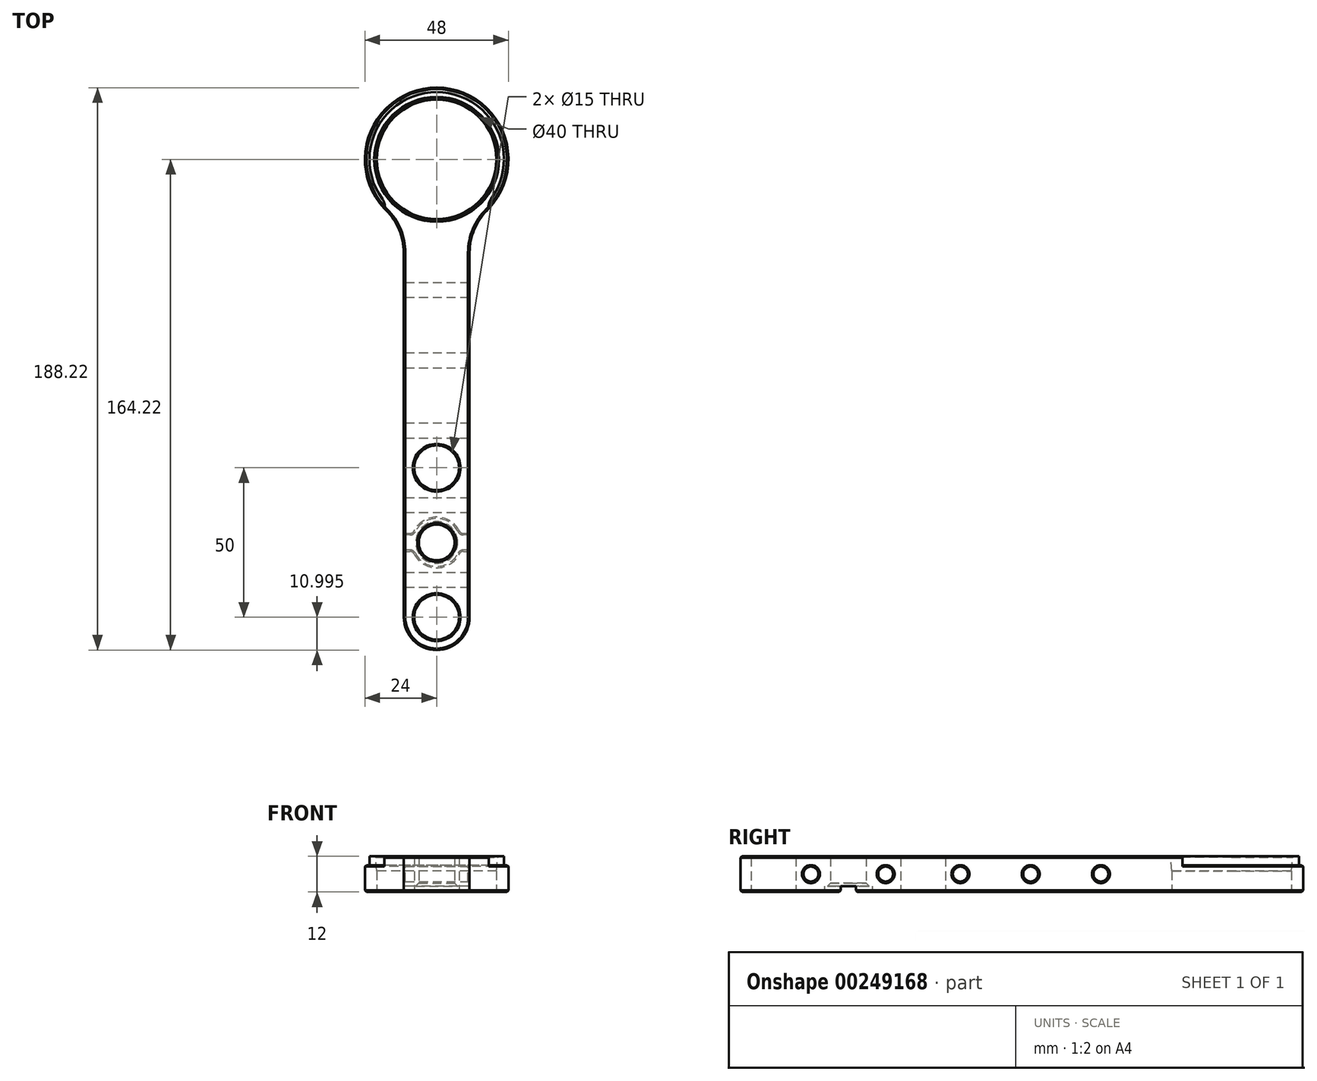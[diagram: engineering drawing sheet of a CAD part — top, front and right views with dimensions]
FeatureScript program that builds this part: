
annotation { "Feature Type Name" : "Feature", "Feature Type Description" : "" }
export const myFeature = defineFeature(function(context is Context, id is Id, definition is map)
    precondition{}
    {
        {
            var Q0;
            Q0=qCreatedBy(makeId("Top.planeOp"),FACE);
            var sketch = newSketch(context, id + "F0", { "sketchPlane" : qUnion([Q0])});
            skArc(sketch, "E0", {"start": v(0, 24) * mm, "mid": v(-22.19, 9.14) * mm, "end": v(-16.9, -17.03) * mm});
            skArc(sketch, "E1", {"start": v(0, 20) * mm, "mid": v(-20, 0) * mm, "end": v(0, -20) * mm});
            skLineSegment(sketch, "E2", {"start": v(0, 0) * mm, "end": v(0, 24) * mm, "construction": true});
            skArc(sketch, "E3.MirrorCS", {"start": v(0, 24) * mm, "mid": v(23.32, 5.66) * mm, "end": v(11, -21.33) * mm});
            skLineSegment(sketch, "E4.top", {"start": v(11, -91.22) * mm, "end": v(-11, -91.22) * mm, "construction": true});
            skLineSegment(sketch, "E4.left", {"start": v(11, -31.22) * mm, "end": v(11, -91.22) * mm});
            skLineSegment(sketch, "E4.right", {"start": v(-11, -31.22) * mm, "end": v(-11, -91.22) * mm});
            skArc(sketch, "E5.trimOffspring", {"start": v(-11, -21.33) * mm, "mid": v(-23.32, 5.66) * mm, "end": v(0, 24) * mm});
            skArc(sketch, "E6.trimOffspring", {"start": v(16.9, -17.03) * mm, "mid": v(22.19, 9.14) * mm, "end": v(0, 24) * mm});
            skPoint(sketch, "E7.visualSharp", {"position": v(-11, -21.33) * mm});
            skArc(sketch, "E7.filletArc", {"start": v(-11, -31.22) * mm, "mid": v(-12.54, -23.54) * mm, "end": v(-16.9, -17.03) * mm});
            skPoint(sketch, "E8.visualSharp", {"position": v(11, -21.33) * mm});
            skArc(sketch, "E8.filletArc", {"start": v(16.9, -17.03) * mm, "mid": v(12.54, -23.54) * mm, "end": v(11, -31.22) * mm});
            skLineSegment(sketch, "E9", {"start": v(-11, -91.22) * mm, "end": v(-11, -153.22) * mm});
            skLineSegment(sketch, "E10", {"start": v(-11, -164.22) * mm, "end": v(11, -164.22) * mm, "construction": true});
            skLineSegment(sketch, "E11", {"start": v(11, -153.22) * mm, "end": v(11, -91.22) * mm});
            skLineSegment(sketch, "E12", {"start": v(0, -91.22) * mm, "end": v(0, -103.22) * mm, "construction": true});
            skPoint(sketch, "E12.endSnap0", {"position": v(0, -91.22) * mm});
            skLineSegment(sketch, "E13", {"start": v(0, -103.22) * mm, "end": v(0, -128.22) * mm, "construction": true});
            skLineSegment(sketch, "E14", {"start": v(0, -128.22) * mm, "end": v(0, -153.22) * mm, "construction": true});
            skCircle(sketch, "E15", {"center": v(0, -103.22) * mm, "radius": 7.5 * mm});
            skCircle(sketch, "E16", {"center": v(0, -153.22) * mm, "radius": 7.5 * mm});
            skPoint(sketch, "E17", {"position": v(0, -128.22) * mm});
            skArc(sketch, "E18", {"start": v(-11, -153.22) * mm, "mid": v(0, -164.22) * mm, "end": v(11, -153.22) * mm});
            skCircle(sketch, "E19", {"center": v(0, -128.22) * mm, "radius": 6 * mm});
            skArc(sketch, "E20.trimOffspring", {"start": v(0, -20) * mm, "mid": v(20, 0) * mm, "end": v(0, 20) * mm});
            skSolve(sketch);
        }
        {
            var Q0;
            Q0 = qSketchRegion(id + "F0", true);
            extrude(context, id + "F1", {"entities" : qUnion([Q0]), "depth" : 12 * mm});
        }
        {
            var Q0;
            Q0=makeQuery(id+"F1.opExtrude","CAP_FACE",FACE,{"disambiguationData":[OSD([sQuery(id+"F0.wireOp",EDGE,"E1"),sQuery(id+"F0.wireOp",EDGE,"F11VOZdt-HZaE-PrO8-QXOm-NcNPcNM7g2nS"),sQuery(id+"F0.wireOp",EDGE,"7m6biw3m-Naaw-kAyD-0goq-zmuKVY0ows0u"),sQuery(id+"F0.wireOp",EDGE,"G1YBRX1K-NmOF-07IS-Nktl-OATFWiHAXenz"),sQuery(id+"F0.wireOp",EDGE,"hBhdh0xz-QFaw-vZRR-R82u-J2mHWQ1tEoxB"),sQuery(id+"F0.wireOp",EDGE,"4GYq8nPm-MSU2-L5ly-pOQU-XlYa1snlLOT1"),sQuery(id+"F0.wireOp",EDGE,"5b97e5dd-33e6-46e9-ad2f-97bc99eada040.MirrorCS"),sQuery(id+"F0.wireOp",EDGE,"66a7403b-aaa3-430a-aa9c-4d805a2a6571.filletArc"),sQuery(id+"F0.wireOp",EDGE,"590532eb-86fd-4acb-be48-ccb052db704c0.MirrorCS"),sQuery(id+"F0.wireOp",EDGE,"590532eb-86fd-4acb-be48-ccb052db704c1.MirrorCS"),sQuery(id+"F0.wireOp",EDGE,"590532eb-86fd-4acb-be48-ccb052db704c2.MirrorCS"),sQuery(id+"F0.wireOp",EDGE,"E4.left"),sQuery(id+"F0.wireOp",EDGE,"E4.right"),sQuery(id+"F0.wireOp",EDGE,"E5.trimOffspring"),sQuery(id+"F0.wireOp",EDGE,"E6.trimOffspring"),sQuery(id+"F0.wireOp",EDGE,"E7.filletArc"),sQuery(id+"F0.wireOp",EDGE,"E8.filletArc"),sQuery(id+"F0.wireOp",EDGE,"hVl1QJwe-WGIT-E3Vb-sIqQ-Org49luiiU1L"),sQuery(id+"F0.wireOp",EDGE,"RhKCMcoN-Tlb7-Fdfj-C25j-MJXdhs9Hkapj"),sQuery(id+"F0.wireOp",EDGE,"e7db96c7-a496-40cb-990f-c2bc624000a7.filletArc"),sQuery(id+"F0.wireOp",EDGE,"6e5d30ee-a383-402b-9502-18f5dfbbc3d4.filletArc"),sQuery(id+"F0.wireOp",EDGE,"84aa8a40-830a-48e8-b378-ae887539fea9.filletArc"),sQuery(id+"F0.wireOp",EDGE,"14e901df-0e15-4e2a-a9a4-94171d117690.filletArc"),sQuery(id+"F0.wireOp",EDGE,"E9"),sQuery(id+"F0.wireOp",EDGE,"E11"),sQuery(id+"F0.wireOp",EDGE,"E15"),sQuery(id+"F0.wireOp",EDGE,"E16"),sQuery(id+"F0.wireOp",EDGE,"E18"),sQuery(id+"F0.wireOp",EDGE,"6ob9XfS0-yGTy-x8Je-VqFr-UpD2jaWEwsn2"),sQuery(id+"F0.wireOp",EDGE,"30e95dc9-bb07-4fe0-ab97-fd2e4bf701961.MirrorCS"),sQuery(id+"F0.wireOp",EDGE,"E19")])],"isStart":true});
            var sketch = newSketch(context, id + "F2", { "sketchPlane" : qUnion([Q0])});
            skCircle(sketch, "E21.0", {"center": v(0, 128.22) * mm, "radius": 8 * mm});
            skSolve(sketch);
        }
        {
            var Q0;
            Q0 = qSketchRegion(id + "F2", true);
            extrude(context, id + "F3", {"entities" : qUnion([Q0]), "operationType" : NewBodyOperationType.REMOVE, "oppositeDirection" : true, "depth" : 2 * mm});
        }
        {
            var Q0;
            Q0=qCreatedBy(makeId("Top.planeOp"),FACE);
            var sketch = newSketch(context, id + "F4", { "sketchPlane" : qUnion([Q0])});
            skLineSegment(sketch, "E22", {"start": v(0, -153.22) * mm, "end": v(0, -128.22) * mm, "construction": true});
            skLineSegment(sketch, "E23", {"start": v(0, -128.22) * mm, "end": v(0, -103.22) * mm, "construction": true});
            skPoint(sketch, "E24", {"position": v(0, -115.72) * mm});
            skPoint(sketch, "E25", {"position": v(0, -140.72) * mm});
            skLineSegment(sketch, "E26", {"start": v(-11, -31.22) * mm, "end": v(11, -31.22) * mm, "construction": true});
            skLineSegment(sketch, "E27", {"start": v(0, -103.22) * mm, "end": v(0, -31.22) * mm, "construction": true});
            skLineSegment(sketch, "E28", {"start": v(0, -103.22) * mm, "end": v(11, -103.22) * mm, "construction": true});
            skPoint(sketch, "E29.MirrorP", {"position": v(0, -90.72) * mm});
            skPoint(sketch, "E30", {"position": v(0, -43.72) * mm});
            skPoint(sketch, "E31", {"position": v(0, -67.22) * mm});
            skSolve(sketch);
        }
        {
            var Q0;
            Q0=qCreatedBy(makeId("Right.planeOp"),FACE);
            var sketch = newSketch(context, id + "F5", { "sketchPlane" : qUnion([Q0])});
            skLineSegment(sketch, "E32", {"start": v(-140.72, 0) * mm, "end": v(-140.72, 6) * mm, "construction": true});
            skLineSegment(sketch, "E33", {"start": v(-115.72, 0) * mm, "end": v(-115.72, 6) * mm, "construction": true});
            skLineSegment(sketch, "E34", {"start": v(-90.72, 0) * mm, "end": v(-90.72, 6) * mm, "construction": true});
            skLineSegment(sketch, "E35", {"start": v(-67.22, 0) * mm, "end": v(-67.22, 6) * mm, "construction": true});
            skLineSegment(sketch, "E36", {"start": v(-43.72, 0) * mm, "end": v(-43.72, 6) * mm, "construction": true});
            skLineSegment(sketch, "E37", {"start": v(-43.72, 6) * mm, "end": v(-67.22, 6) * mm, "construction": true});
            skLineSegment(sketch, "E38", {"start": v(-90.72, 6) * mm, "end": v(-67.22, 6) * mm, "construction": true});
            skLineSegment(sketch, "E39", {"start": v(-90.72, 6) * mm, "end": v(-115.72, 6) * mm, "construction": true});
            skLineSegment(sketch, "E40", {"start": v(-115.72, 6) * mm, "end": v(-140.72, 6) * mm, "construction": true});
            skLineSegment(sketch, "E41", {"start": v(-43.72, 6) * mm, "end": v(-43.72, 12) * mm, "construction": true});
            skPoint(sketch, "E42", {"position": v(-140.72, 6) * mm});
            skPoint(sketch, "E43", {"position": v(-115.72, 6) * mm});
            skPoint(sketch, "E44", {"position": v(-90.72, 6) * mm});
            skPoint(sketch, "E45", {"position": v(-67.22, 6) * mm});
            skPoint(sketch, "E46", {"position": v(-43.72, 6) * mm});
            skCircle(sketch, "E47", {"center": v(-140.72, 6) * mm, "radius": 2.5 * mm});
            skCircle(sketch, "E48", {"center": v(-115.72, 6) * mm, "radius": 2.5 * mm});
            skCircle(sketch, "E49", {"center": v(-90.72, 6) * mm, "radius": 2.5 * mm});
            skCircle(sketch, "E50", {"center": v(-67.22, 6) * mm, "radius": 2.5 * mm});
            skCircle(sketch, "E51", {"center": v(-43.72, 6) * mm, "radius": 2.5 * mm});
            skSolve(sketch);
        }
        {
            var Q0;
            Q0 = qSketchRegion(id + "F5", true);
            extrude(context, id + "F6", {"entities" : qUnion([Q0]), "operationType" : NewBodyOperationType.REMOVE, "endBound" : BoundingType.UP_TO_NEXT, "oppositeDirection" : true, "depth" : 25 * mm, "offsetDistance" : 25 * mm, "hasSecondDirection" : true, "secondDirectionBound" : SecondDirectionBoundingType.UP_TO_NEXT, "secondDirectionOppositeDirection" : false, "secondDirectionDepth" : 25 * mm});
        }
        {
            var Q0;
            Q0=makeQuery(id+"F1.opExtrude","CAP_FACE",FACE,{"disambiguationData":[OSD([sQuery(id+"F0.wireOp",EDGE,"E1"),sQuery(id+"F0.wireOp",EDGE,"E4.left"),sQuery(id+"F0.wireOp",EDGE,"E4.right"),sQuery(id+"F0.wireOp",EDGE,"E5.trimOffspring"),sQuery(id+"F0.wireOp",EDGE,"E6.trimOffspring"),sQuery(id+"F0.wireOp",EDGE,"E7.filletArc"),sQuery(id+"F0.wireOp",EDGE,"E8.filletArc"),sQuery(id+"F0.wireOp",EDGE,"E9"),sQuery(id+"F0.wireOp",EDGE,"E11"),sQuery(id+"F0.wireOp",EDGE,"E15"),sQuery(id+"F0.wireOp",EDGE,"E16"),sQuery(id+"F0.wireOp",EDGE,"E18"),sQuery(id+"F0.wireOp",EDGE,"E19"),sQuery(id+"F0.wireOp",EDGE,"E20.trimOffspring")])],"isStart":true});
            var sketch = newSketch(context, id + "F7", { "sketchPlane" : qUnion([Q0])});
            skLineSegment(sketch, "E52.bottom", {"start": v(-11, 125.72) * mm, "end": v(11, 125.72) * mm});
            skLineSegment(sketch, "E52.top", {"start": v(-11, 130.72) * mm, "end": v(11, 130.72) * mm});
            skLineSegment(sketch, "E52.left", {"start": v(-11, 125.72) * mm, "end": v(-11, 130.72) * mm});
            skLineSegment(sketch, "E52.right", {"start": v(11, 125.72) * mm, "end": v(11, 130.72) * mm});
            skPoint(sketch, "E52.middle", {"position": v(0, 128.22) * mm});
            skSolve(sketch);
        }
        {
            var Q0;
            Q0 = qSketchRegion(id + "F7", true);
            var Q1;
            {var subQ0=sQuery(id+"F7.wireOp",EDGE,"E52.top");var subQ1=makeQuery(id+"F3.boolean.opBoolean","COPY",EDGE,{"derivedFrom":makeQuery(id+"F3.opExtrude","CAP_EDGE",EDGE,{"disambiguationData":[OSD([sQuery(id+"F2.wireOp",EDGE,"E21.0")])],"isStart":true})});var subQ2=makeQuery(id+"F7.imprint","INTERSECT",VERTEX,{"disambiguationData":[OD(0.0)],"derivedFrom":[subQ1,subQ0]});Q1=makeQuery(id+"F7.imprint","IMPRINT",FACE,{"disambiguationData":[TD([[makeQuery(id+"F7.imprint","IMPRINT",EDGE,{"disambiguationData":[TD([[subQ2,-1.0]])],"derivedFrom":subQ0}),1.0]])]});}
            var Q2;
            Q2=makeQuery(id+"F3.boolean.opBoolean","COPY",FACE,{"derivedFrom":makeQuery(id+"F3.opExtrude","CAP_FACE",FACE,{"disambiguationData":[OSD([sQuery(id+"F2.wireOp",EDGE,"E21.0")])],"isStart":false})});
            extrude(context, id + "F8", {"entities" : qUnion([Q0, Q1]), "operationType" : NewBodyOperationType.REMOVE, "endBound" : BoundingType.UP_TO_SURFACE, "oppositeDirection" : true, "depth" : 25 * mm, "endBoundEntityFace" : qUnion([Q2]), "offsetDistance" : 25 * mm});
        }
        {
            var Q0;
            Q0=makeQuery(id+"F1.opExtrude","CAP_FACE",FACE,{"disambiguationData":[OSD([sQuery(id+"F0.wireOp",EDGE,"E0"),sQuery(id+"F0.wireOp",EDGE,"E1"),sQuery(id+"F0.wireOp",EDGE,"E3.MirrorCS"),sQuery(id+"F0.wireOp",EDGE,"E4.left"),sQuery(id+"F0.wireOp",EDGE,"E4.right"),sQuery(id+"F0.wireOp",EDGE,"E7.filletArc"),sQuery(id+"F0.wireOp",EDGE,"E8.filletArc"),sQuery(id+"F0.wireOp",EDGE,"E9"),sQuery(id+"F0.wireOp",EDGE,"E11"),sQuery(id+"F0.wireOp",EDGE,"E15"),sQuery(id+"F0.wireOp",EDGE,"E16"),sQuery(id+"F0.wireOp",EDGE,"E18"),sQuery(id+"F0.wireOp",EDGE,"E19"),sQuery(id+"F0.wireOp",EDGE,"E20.trimOffspring")])],"isStart":false});
            var sketch = newSketch(context, id + "F9", { "sketchPlane" : qUnion([Q0])});
            skArc(sketch, "E53.0", {"start": v(18.13, -13.33) * mm, "mid": v(0, 22.5) * mm, "end": v(-18.13, -13.33) * mm});
            skLineSegment(sketch, "E54", {"start": v(0, 0) * mm, "end": v(-15.9, -15.9) * mm, "construction": true});
            skLineSegment(sketch, "E55", {"start": v(0, 0) * mm, "end": v(0, 20) * mm, "construction": true});
            skLineSegment(sketch, "E56.MirrorCS", {"start": v(0, 0) * mm, "end": v(15.9, -15.9) * mm, "construction": true});
            skLineSegment(sketch, "E57", {"start": v(15.9, -15.9) * mm, "end": v(18.52, -18.52) * mm, "construction": true});
            skArc(sketch, "E58", {"start": v(18.13, -13.33) * mm, "mid": v(17.36, -16) * mm, "end": v(18.52, -18.52) * mm});
            skArc(sketch, "E59.MirrorCS", {"start": v(-18.13, -13.33) * mm, "mid": v(-17.36, -16) * mm, "end": v(-18.52, -18.52) * mm});
            skArc(sketch, "E60", {"start": v(18.52, -18.52) * mm, "mid": v(0, 26.2) * mm, "end": v(-18.52, -18.52) * mm});
            skSolve(sketch);
        }
        {
            var Q0;
            Q0 = qSketchRegion(id + "F9", true);
            extrude(context, id + "F10", {"entities" : qUnion([Q0]), "operationType" : NewBodyOperationType.REMOVE, "oppositeDirection" : true, "depth" : 3 * mm, "offsetDistance" : 25 * mm});
        }
        {
            var Q0;
            {var subQ0=sQuery(id+"F7.wireOp",EDGE,"E52.top");var subQ1=sQuery(id+"F2.wireOp",EDGE,"E21.0");Q0=makeQuery(id+"F8.boolean.opBoolean","COPY",EDGE,{"derivedFrom":makeQuery(id+"F8.opExtrude","SWEPT_EDGE",EDGE,{"disambiguationData":[OSD([subQ1,subQ0]),TDD([makeQuery(id+"F7.imprint","INTERSECT",VERTEX,{"disambiguationData":[OD(1.0)],"derivedFrom":[makeQuery(id+"F3.boolean.opBoolean","COPY",EDGE,{"derivedFrom":makeQuery(id+"F3.opExtrude","CAP_EDGE",EDGE,{"disambiguationData":[OSD([subQ1])],"isStart":true})}),subQ0]})])]})});}
            var Q1;
            Q1=makeQuery(id+"F8.boolean.opBoolean","INTERSECT",EDGE,{"disambiguationData":[OD(1.0)],"derivedFrom":[makeQuery(id+"F3.boolean.opBoolean","COPY",FACE,{"derivedFrom":makeQuery(id+"F3.opExtrude","SWEPT_FACE",FACE,{"disambiguationData":[OSD([sQuery(id+"F2.wireOp",EDGE,"E21.0")])]})}),makeQuery(id+"F8.opExtrude","SWEPT_FACE",FACE,{"disambiguationData":[OSD([sQuery(id+"F7.wireOp",EDGE,"E52.bottom")])]})]});
            var Q2;
            {var subQ0=sQuery(id+"F7.wireOp",EDGE,"E52.top");var subQ1=sQuery(id+"F2.wireOp",EDGE,"E21.0");Q2=makeQuery(id+"F8.boolean.opBoolean","COPY",EDGE,{"derivedFrom":makeQuery(id+"F8.opExtrude","SWEPT_EDGE",EDGE,{"disambiguationData":[OSD([subQ1,subQ0]),TDD([makeQuery(id+"F7.imprint","INTERSECT",VERTEX,{"disambiguationData":[OD(0.0)],"derivedFrom":[makeQuery(id+"F3.boolean.opBoolean","COPY",EDGE,{"derivedFrom":makeQuery(id+"F3.opExtrude","CAP_EDGE",EDGE,{"disambiguationData":[OSD([subQ1])],"isStart":true})}),subQ0]})])]})});}
            var Q3;
            Q3=makeQuery(id+"F8.boolean.opBoolean","INTERSECT",EDGE,{"disambiguationData":[OD(0.0)],"derivedFrom":[makeQuery(id+"F3.boolean.opBoolean","COPY",FACE,{"derivedFrom":makeQuery(id+"F3.opExtrude","SWEPT_FACE",FACE,{"disambiguationData":[OSD([sQuery(id+"F2.wireOp",EDGE,"E21.0")])]})}),makeQuery(id+"F8.opExtrude","SWEPT_FACE",FACE,{"disambiguationData":[OSD([sQuery(id+"F7.wireOp",EDGE,"E52.bottom")])]})]});
            fillet(context, id + "F11", {"entities" : qUnion([Q0, Q1, Q2, Q3]), "radius" : 2 * mm, "tangentPropagation" : true, "allowEdgeOverflow" : false});
        }
        {
            var Q0;
            Q0=makeQuery(id+"F1.opExtrude","CAP_FACE",FACE,{"disambiguationData":[OSD([sQuery(id+"F0.wireOp",EDGE,"E1"),sQuery(id+"F0.wireOp",EDGE,"E4.left"),sQuery(id+"F0.wireOp",EDGE,"E4.right"),sQuery(id+"F0.wireOp",EDGE,"E5.trimOffspring"),sQuery(id+"F0.wireOp",EDGE,"E6.trimOffspring"),sQuery(id+"F0.wireOp",EDGE,"E7.filletArc"),sQuery(id+"F0.wireOp",EDGE,"E8.filletArc"),sQuery(id+"F0.wireOp",EDGE,"E9"),sQuery(id+"F0.wireOp",EDGE,"E11"),sQuery(id+"F0.wireOp",EDGE,"E15"),sQuery(id+"F0.wireOp",EDGE,"E16"),sQuery(id+"F0.wireOp",EDGE,"E18"),sQuery(id+"F0.wireOp",EDGE,"E19"),sQuery(id+"F0.wireOp",EDGE,"E20.trimOffspring")])],"isStart":true});
            var Q1;
            Q1=makeQuery(id+"F6.boolean.opBoolean","COPY",FACE,{"derivedFrom":makeQuery(id+"F6.opExtrude","SWEPT_FACE",FACE,{"disambiguationData":[OSD([sQuery(id+"F5.wireOp",EDGE,"E47")])]})});
            var Q2;
            Q2=makeQuery(id+"F6.boolean.opBoolean","COPY",FACE,{"derivedFrom":makeQuery(id+"F6.opExtrude","SWEPT_FACE",FACE,{"disambiguationData":[OSD([sQuery(id+"F5.wireOp",EDGE,"E48")])]})});
            var Q3;
            Q3=makeQuery(id+"F6.boolean.opBoolean","COPY",FACE,{"derivedFrom":makeQuery(id+"F6.opExtrude","SWEPT_FACE",FACE,{"disambiguationData":[OSD([sQuery(id+"F5.wireOp",EDGE,"E49")])]})});
            var Q4;
            Q4=makeQuery(id+"F6.boolean.opBoolean","COPY",FACE,{"derivedFrom":makeQuery(id+"F6.opExtrude","SWEPT_FACE",FACE,{"disambiguationData":[OSD([sQuery(id+"F5.wireOp",EDGE,"E50")])]})});
            var Q5;
            Q5=makeQuery(id+"F6.boolean.opBoolean","COPY",FACE,{"derivedFrom":makeQuery(id+"F6.opExtrude","SWEPT_FACE",FACE,{"disambiguationData":[OSD([sQuery(id+"F5.wireOp",EDGE,"E51")])]})});
            var Q6;
            Q6=makeQuery(id+"F1.opExtrude","CAP_EDGE",EDGE,{"disambiguationData":[OSD([sQuery(id+"F0.wireOp",EDGE,"E1"),sQuery(id+"F0.wireOp",EDGE,"E20.trimOffspring")])],"isStart":true});
            var Q7;
            Q7=makeQuery(id+"F1.opExtrude","CAP_EDGE",EDGE,{"disambiguationData":[OSD([sQuery(id+"F0.wireOp",EDGE,"E7.filletArc")])],"isStart":false});
            var Q8;
            Q8=makeQuery(id+"F1.opExtrude","CAP_EDGE",EDGE,{"disambiguationData":[OSD([sQuery(id+"F0.wireOp",EDGE,"E15")])],"isStart":false});
            var Q9;
            Q9=makeQuery(id+"F1.opExtrude","CAP_EDGE",EDGE,{"disambiguationData":[OSD([sQuery(id+"F0.wireOp",EDGE,"E16")])],"isStart":false});
            var Q10;
            Q10=makeQuery(id+"F8.boolean.opBoolean","COPY",EDGE,{"derivedFrom":makeQuery(id+"F8.opExtrude","SWEPT_EDGE",EDGE,{"disambiguationData":[OSD([sQuery(id+"F0.wireOp",EDGE,"E4.right"),sQuery(id+"F0.wireOp",EDGE,"E9"),sQuery(id+"F7.wireOp",EDGE,"E52.top"),sQuery(id+"F7.wireOp",EDGE,"E52.left")])]})});
            var Q11;
            Q11=makeQuery(id+"F8.boolean.opBoolean","COPY",EDGE,{"derivedFrom":makeQuery(id+"F8.opExtrude","CAP_EDGE",EDGE,{"disambiguationData":[OSD([sQuery(id+"F7.wireOp",EDGE,"E52.left")])],"isStart":false})});
            var Q12;
            Q12=makeQuery(id+"F8.boolean.opBoolean","COPY",EDGE,{"derivedFrom":makeQuery(id+"F8.opExtrude","SWEPT_EDGE",EDGE,{"disambiguationData":[OSD([sQuery(id+"F0.wireOp",EDGE,"E4.right"),sQuery(id+"F0.wireOp",EDGE,"E9"),sQuery(id+"F7.wireOp",EDGE,"E52.bottom"),sQuery(id+"F7.wireOp",EDGE,"E52.left")])]})});
            var Q13;
            Q13=makeQuery(id+"F8.boolean.opBoolean","COPY",EDGE,{"derivedFrom":makeQuery(id+"F8.opExtrude","SWEPT_EDGE",EDGE,{"disambiguationData":[OSD([sQuery(id+"F0.wireOp",EDGE,"E4.left"),sQuery(id+"F0.wireOp",EDGE,"E11"),sQuery(id+"F7.wireOp",EDGE,"E52.top"),sQuery(id+"F7.wireOp",EDGE,"E52.right")])]})});
            var Q14;
            Q14=makeQuery(id+"F8.boolean.opBoolean","COPY",EDGE,{"derivedFrom":makeQuery(id+"F8.opExtrude","CAP_EDGE",EDGE,{"disambiguationData":[OSD([sQuery(id+"F7.wireOp",EDGE,"E52.right")])],"isStart":false})});
            var Q15;
            Q15=makeQuery(id+"F8.boolean.opBoolean","COPY",EDGE,{"derivedFrom":makeQuery(id+"F8.opExtrude","SWEPT_EDGE",EDGE,{"disambiguationData":[OSD([sQuery(id+"F0.wireOp",EDGE,"E4.left"),sQuery(id+"F0.wireOp",EDGE,"E11"),sQuery(id+"F7.wireOp",EDGE,"E52.bottom"),sQuery(id+"F7.wireOp",EDGE,"E52.right")])]})});
            var Q16;
            Q16=makeQuery(id+"F1.opExtrude","CAP_EDGE",EDGE,{"disambiguationData":[OSD([sQuery(id+"F0.wireOp",EDGE,"E19")])],"isStart":false});
            var Q17;
            Q17=makeQuery(id+"F10.boolean.opBoolean","COPY",EDGE,{"derivedFrom":makeQuery(id+"F10.opExtrude","CAP_EDGE",EDGE,{"disambiguationData":[OSD([sQuery(id+"F9.wireOp",EDGE,"E53.0")])],"isStart":true})});
            var Q18;
            Q18=makeQuery(id+"F10.boolean.opBoolean","INTERSECT",EDGE,{"derivedFrom":[makeQuery(id+"F1.opExtrude","SWEPT_FACE",FACE,{"disambiguationData":[OSD([sQuery(id+"F0.wireOp",EDGE,"E0"),sQuery(id+"F0.wireOp",EDGE,"E3.MirrorCS")])]}),makeQuery(id+"F10.opExtrude","CAP_FACE",FACE,{"disambiguationData":[OSD([sQuery(id+"F9.wireOp",EDGE,"E53.0"),sQuery(id+"F9.wireOp",EDGE,"E58"),sQuery(id+"F9.wireOp",EDGE,"E59.MirrorCS"),sQuery(id+"F9.wireOp",EDGE,"E60")])],"isStart":false})]});
            chamfer(context, id + "F12", {"entities" : qUnion([Q0, Q1, Q2, Q3, Q4, Q5, Q6, Q7, Q8, Q9, Q10, Q11, Q12, Q13, Q14, Q15, Q16, Q17, Q18]), "width" : 0.5 * mm, "tangentPropagation" : true});
        }
        {
            var Q0;
            Q0=makeQuery(id+"F1.opExtrude","CAP_EDGE",EDGE,{"disambiguationData":[OSD([sQuery(id+"F0.wireOp",EDGE,"E1"),sQuery(id+"F0.wireOp",EDGE,"E20.trimOffspring")])],"isStart":false});
            chamfer(context, id + "F13", {"entities" : qUnion([Q0]), "chamferType" : ChamferType.OFFSET_ANGLE, "width" : 5 * mm, "oppositeDirection" : false, "angle" : 5 * degree, "tangentPropagation" : true});
        }
        {
            var Q0;
            {var subQ0=sQuery(id+"F0.wireOp",EDGE,"E20.trimOffspring");var subQ1=sQuery(id+"F0.wireOp",EDGE,"E1");Q0=makeQuery(id+"F13.opChamfer","BLEND_EDGE",EDGE,{"blendedFrom":[makeQuery(id+"F1.opExtrude","CAP_EDGE",EDGE,{"disambiguationData":[OSD([subQ1,subQ0])],"isStart":false}),makeQuery(id+"F1.opExtrude","CAP_FACE",FACE,{"disambiguationData":[OSD([subQ1,sQuery(id+"F0.wireOp",EDGE,"E4.left"),sQuery(id+"F0.wireOp",EDGE,"E4.right"),sQuery(id+"F0.wireOp",EDGE,"E5.trimOffspring"),sQuery(id+"F0.wireOp",EDGE,"E6.trimOffspring"),sQuery(id+"F0.wireOp",EDGE,"E7.filletArc"),sQuery(id+"F0.wireOp",EDGE,"E8.filletArc"),sQuery(id+"F0.wireOp",EDGE,"E9"),sQuery(id+"F0.wireOp",EDGE,"E11"),sQuery(id+"F0.wireOp",EDGE,"E15"),sQuery(id+"F0.wireOp",EDGE,"E16"),sQuery(id+"F0.wireOp",EDGE,"E18"),sQuery(id+"F0.wireOp",EDGE,"E19"),subQ0])],"isStart":false})],"blendedInto":[makeQuery(id+"F1.opExtrude","CAP_FACE",FACE,{"disambiguationData":[OSD([subQ1,sQuery(id+"F0.wireOp",EDGE,"E4.left"),sQuery(id+"F0.wireOp",EDGE,"E4.right"),sQuery(id+"F0.wireOp",EDGE,"E5.trimOffspring"),sQuery(id+"F0.wireOp",EDGE,"E6.trimOffspring"),sQuery(id+"F0.wireOp",EDGE,"E7.filletArc"),sQuery(id+"F0.wireOp",EDGE,"E8.filletArc"),sQuery(id+"F0.wireOp",EDGE,"E9"),sQuery(id+"F0.wireOp",EDGE,"E11"),sQuery(id+"F0.wireOp",EDGE,"E15"),sQuery(id+"F0.wireOp",EDGE,"E16"),sQuery(id+"F0.wireOp",EDGE,"E18"),sQuery(id+"F0.wireOp",EDGE,"E19"),subQ0])],"isStart":false})]});}
            chamfer(context, id + "F14", {"entities" : qUnion([Q0]), "width" : 0.5 * mm, "tangentPropagation" : true});
        }
        {
            var Q0;
            Q0=makeQuery(id+"F3.boolean.opBoolean","INTERSECT",EDGE,{"derivedFrom":[makeQuery(id+"F1.opExtrude","SWEPT_FACE",FACE,{"disambiguationData":[OSD([sQuery(id+"F0.wireOp",EDGE,"E19")])]}),makeQuery(id+"F3.opExtrude","CAP_FACE",FACE,{"disambiguationData":[OSD([sQuery(id+"F2.wireOp",EDGE,"E21.0")])],"isStart":false})]});
            chamfer(context, id + "F15", {"entities" : qUnion([Q0]), "chamferType" : ChamferType.TWO_OFFSETS, "width1" : 1 * mm, "oppositeDirection" : false, "width2" : 1 * mm, "tangentPropagation" : true});
        }
    });
